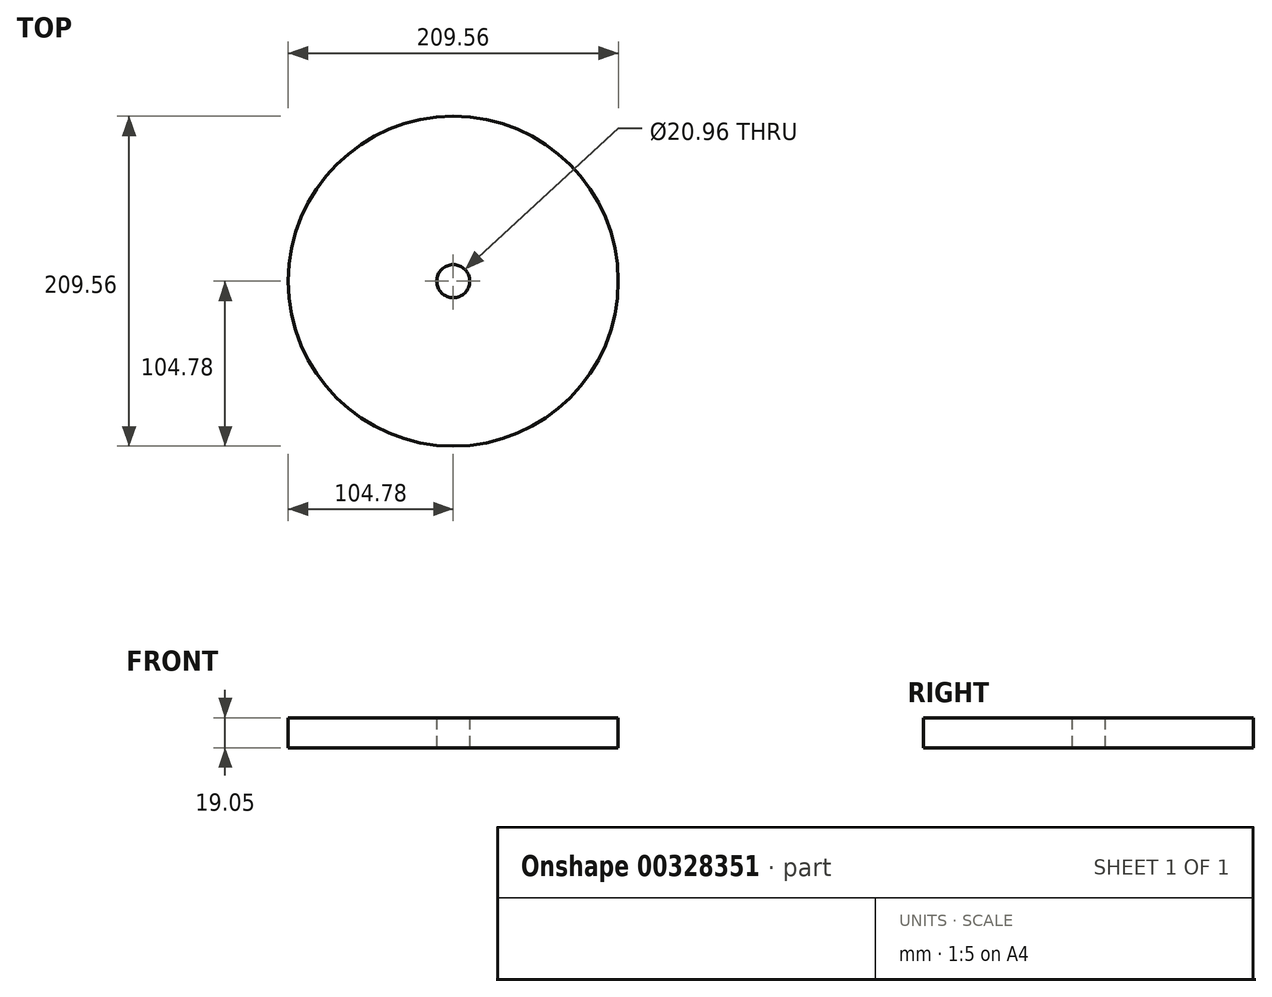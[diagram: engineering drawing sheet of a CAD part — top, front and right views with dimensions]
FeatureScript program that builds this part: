
annotation { "Feature Type Name" : "Feature", "Feature Type Description" : "" }
export const myFeature = defineFeature(function(context is Context, id is Id, definition is map)
    precondition{}
    {
        {
            var Q0;
            Q0=qCreatedBy(makeId("Top.planeOp"),FACE);
            var sketch = newSketch(context, id + "F0", { "sketchPlane" : qUnion([Q0])});
            skCircle(sketch, "E0", {"center": v(0, 0) * mm, "radius": 104.77 * mm});
            skCircle(sketch, "E1", {"center": v(0, 0) * mm, "radius": 10.48 * mm});
            skSolve(sketch);
        }
        {
            var Q0;
            Q0=makeQuery(id+"F0.imprint","IMPRINT",FACE,{"disambiguationData":[TD([[makeQuery(id+"F0.imprint","IMPRINT",EDGE,{"derivedFrom":sQuery(id+"F0.wireOp",EDGE,"E0")}),1.0]])]});
            extrude(context, id + "F1", {"entities" : qUnion([Q0]), "depth" : 19.05 * mm});
        }
    });
